# Revit family: BIMLIB_ПланкаПримыканиеНижнееКТрубеФальц_GRANDLINE
name_source: partatom
category: Обобщенные модели
revit_build: Autodesk Revit 2017 (Build: 20160225_1515(x64)
units: mm (PartAtom-declared; Revit-internal decimal feet)

## family parameters
Может служить основой для арматурных стержней = Нет
Общий = Нет
При загрузке вырезать с полостями = Нет
Размер круглого соединителя = Использовать диаметр
Тип детали = Нормальный
Точка расчета площади = Нет

## types (2) — shared parameters
ADSK_Версия Revit = 2017
ADSK_Завод-изготовитель = Grand Line
ADSK_Код изделия = М.15.025.005
ADSK_Материал = GL_Сталь_RAL9005
ADSK_Наименование = Планка примыкание нижнее к трубе фальц
ADSK_Обозначение = ГОСТ 19904-90, ГОСТ 14918-80
BL_BIM library = https://bimlib.pro
URL = https://www.grandline.ru
Изготовитель = Grand Line
Описание = Планка примыкание нижнее к трубе фальц

## per-type parameters (varying)
| type | Стык_Конверт | Стык_Упрощенный |
| Стык упрощенный | Нет | Да |
| Стык конверт | Да | Нет |
